# Revit family: EdgeProtection_Gutters_Schluter_Bara_Esot
name_source: partatom
category: Profiles
units: mm (PartAtom-declared; Revit-internal decimal feet)

## family parameters
OmniClass Number = 23.35.50.11.21.17
OmniClass Title = Underlays, Linings, Separations
Profile Usage = <Generic>
Rotate with component = No
Section Shape = Not Defined

## types (2) — shared parameters
Assembly Code = C3020430
Construction Details = http://www.arcat.com
Description = As Specified in 09 30 00
Green Building-LEED = http://www.arcat.com
Installation-Fabrication = http://www.schluter.com
Keynote = 09 30 00
Manufacturer = Schluter System LP
Manufacturer Fax = 800-477-9783
Manufacturer Website = http://www.schluter.com
Model = As Specified in 09 30 00
Product Data = http://www.arcat.com
Product Properties = http://www.arcat.com
Sales Information = http://www.schluter.com
Send Message = http://www.arcat.com
SpecWizard = http://www.arcat.com
Specification = http://www.arcat.com
Test Data = http://www.schluter.com
URL = http://www.schluter.com
zero-valued in all types: Expected Lifespan (Years), Maintenance Schedule (Months), Warranty Duration (Years)

## per-type parameters (varying)
| type | H |
| 4.375in | 0' - 4 3/8" |
| 2.375in | 0' - 2 3/8" |

## geometry (parser evidence)
native form markers: Sweep x1
no freeform markers — native parametric forms only
